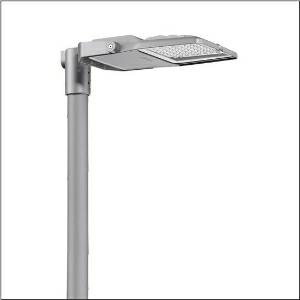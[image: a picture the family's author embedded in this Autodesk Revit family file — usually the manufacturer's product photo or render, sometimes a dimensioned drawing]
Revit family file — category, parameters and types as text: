
# Revit family: floodlight_fl_21_iq_mini___pl64_5xa7772c2e3a_d31a
name_source: partatom
category: Lighting Fixtures
units: mm (PartAtom-declared; Revit-internal decimal feet)

## family parameters
Cut with Voids When Loaded = No
Host = Face
Light Source = No
Part Type = Normal
Room Calculation Point = No
Round Connector Dimension = Use Diameter
Shared = No

## types (1)
- --- (1 x LED, 11790 lm, 87.2 W, 3000K)
    Apparent Load = 87 VA
    CIE Flux Codes = 28 80 98 100 100
    Color Rendering = 70
    Color Temperature = 3000K
    Default Elevation = 1800 mm
    Description = Floodlight FL 21 iQ mini, floodlight, primary light control with lens, of PMMA, primary optical cover: protective disc, of toughened safety glass, transparent, light distribution: PL64, light emission: direct distribution, installation type: surface-mounted, LED, High Power LED, rated luminous flux: 11.790lm, luminous efficacy: 135lm/W, light colour: 730, colour temperature: 3000K, control gear: iQ Street-Remote/DALI, control: Street-Remote, Auto-Match, Temp-Guard, Night-Set, Smart-Wire, optimised constant luminous flux control (CLO 2.0), Light-Fading, Lumen-Switch, with terminal, 6-pole, mains connection: 220..240V, AC, 50/60Hz, start of lifetime: 87W, end of service life: 92W, reduction: 40W, luminaire housing, of diecast aluminium, powder-coated, Siteco® metallic grey (DB 702S), corrosivity category C5 mid according to DIN EN ISO 12944, suitable for swimming pools, chlorine-resistant, sealing non-destructively replaceable, please order mast flange separately, mast bracket, of steel, galvanised, powder-coated, protection rating (complete): IP66, insulation class (complete): insulation class II (safety insulation), certification: CE, ENEC, VDE, protection symbol: D, impact resistance: IK08, permissible operating ambient temperature: -40..+40°C, permissible operating ambient temperature for outdoor applications: -40..+50°C, standard: DIN EN 12944, LABS conformity tested according to VDMA 24364:2018-05, packaging unit: 1 piece

Light Distribution: PL64
    Height = 70 mm
    Lamp = 1 x LED
    Lamp Light Flux = 11790 lm
    Lamp Power = 87.2 W
    Lamp count = 1
    Length = 485 mm
    Luminous efficacy = 135 lm/W
    Manufacturer = Siteco
    ModVariant = No
    Model = 5XA7772C2E3A
    Number of Poles = 1
    OnlyDefault = Yes
    Power Factor = 1
    Product Name = Floodlight FL 21 iQ mini | PL64
    Product group = floodlight | pylon annexe
    ProductGroupID = 6200
    Protection Class = Protection class II
    Protection Degree = IP 66
    RLX_Detail_Level = 1
    RLX_Emergency_Light_Flux = 0 lm
    RLX_Emergency_Type = 0
    RLX_Emergency_Type_DB = No
    RlxData = <blob elided: 101225 chars, md5=577649af>
    Socket = socket
    Standby Power = 0 W
    System Light Flux = 11790 lm
    System Power = 87 W
    Type Comments = factory setting: luminous flux: 100 % | dim-lin: 254 | 456 mA
    Type Image = l_1007125.jpg
    URL = http://relux.com
    VarID = @adj_166362
    Voltage = 0 V
    Weight = 0.00 kg
    Width = 337 mm

## geometry (parser evidence)
native form markers: Blend x4, Sweep x12
no freeform markers — native parametric forms only
